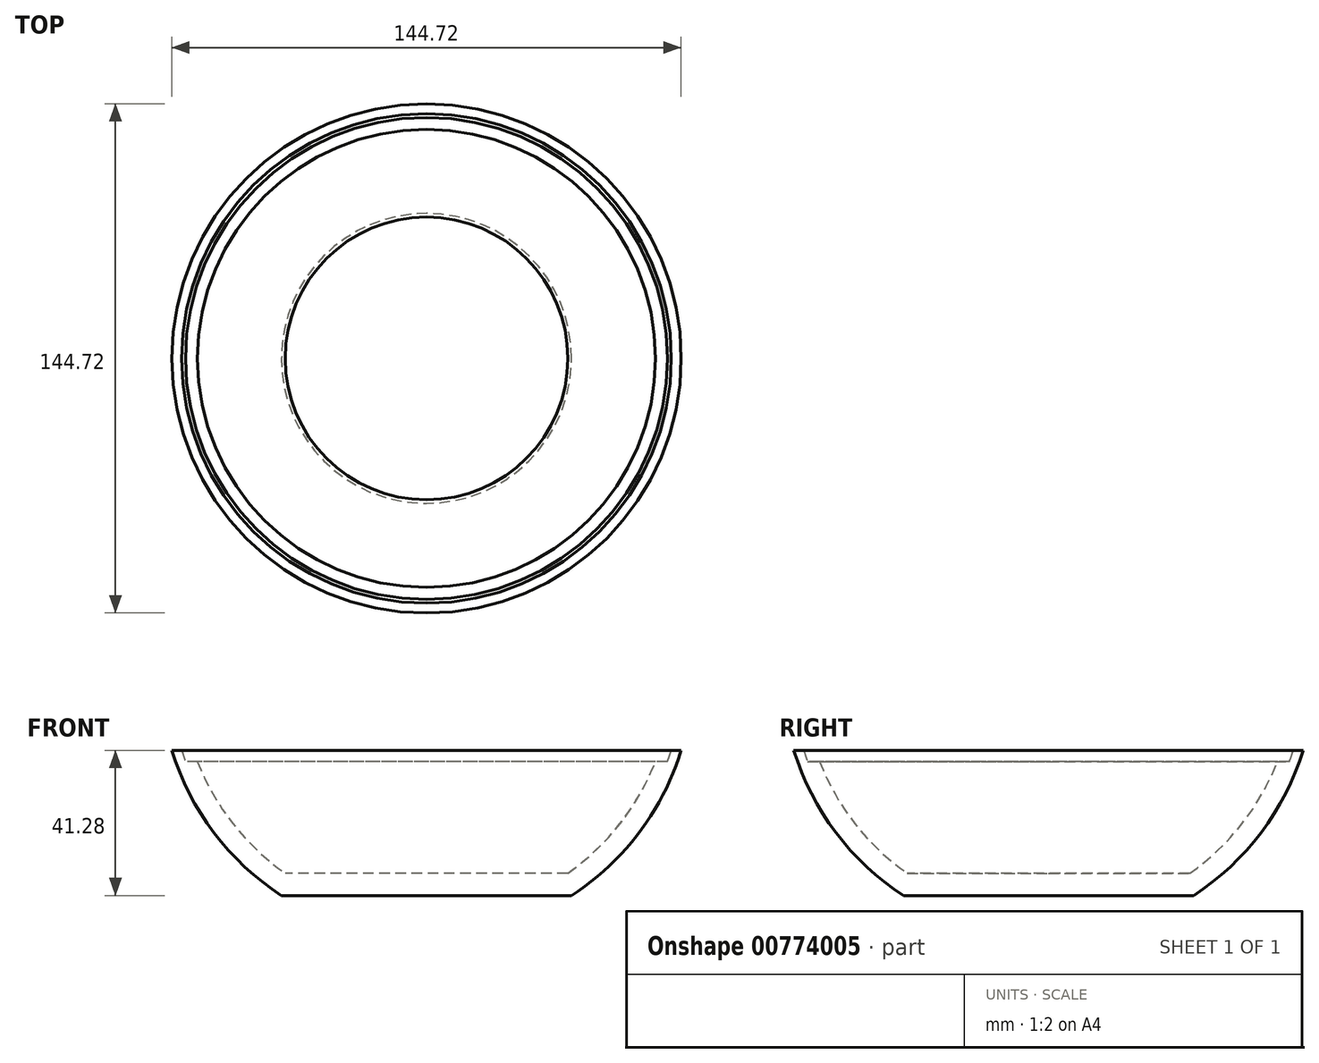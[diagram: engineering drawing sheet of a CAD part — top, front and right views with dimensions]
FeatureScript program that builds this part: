
annotation { "Feature Type Name" : "Feature", "Feature Type Description" : "" }
export const myFeature = defineFeature(function(context is Context, id is Id, definition is map)
    precondition{}
    {
        {
            var Q0;
            Q0=qCreatedBy(makeId("Front.planeOp"),FACE);
            var sketch = newSketch(context, id + "F0", { "sketchPlane" : qUnion([Q0])});
            skArc(sketch, "E0", {"start": v(-72.36, -22.23) * mm, "mid": v(-60.4, -45.6) * mm, "end": v(-41.2, -63.5) * mm});
            skLineSegment(sketch, "E1", {"start": v(-75.7, 0) * mm, "end": v(75.7, 0) * mm, "construction": true});
            skLineSegment(sketch, "E2.0", {"start": v(-72.36, -22.23) * mm, "end": v(-69.56, -22.23) * mm});
            skArc(sketch, "E3.0", {"start": v(-69.56, -22.23) * mm, "mid": v(-69.03, -23.82) * mm, "end": v(-68.47, -25.4) * mm});
            skArc(sketch, "E4.0", {"start": v(-65.07, -25.4) * mm, "mid": v(-54.96, -43.11) * mm, "end": v(-40.16, -57.15) * mm});
            skLineSegment(sketch, "E5.0", {"start": v(-68.47, -25.4) * mm, "end": v(-65.07, -25.4) * mm});
            skLineSegment(sketch, "E6", {"start": v(0, -57.15) * mm, "end": v(0, -63.5) * mm});
            skLineSegment(sketch, "E7.0", {"start": v(-41.2, -63.5) * mm, "end": v(0, -63.5) * mm});
            skLineSegment(sketch, "E8.0", {"start": v(-40.16, -57.15) * mm, "end": v(0, -57.15) * mm});
            skSolve(sketch);
        }
        {
            var Q0;
            Q0 = qSketchRegion(id + "F0", true);
            var Q1;
            Q1=sQuery(id+"F0.wireOp",EDGE,"E6");
            revolve(context, id + "F1", {"surfaceOperationType" : NewSurfaceOperationType.NEW, "entities" : qUnion([Q0]), "axis" : qUnion([Q1]), "revolveType" : RevolveType.FULL});
        }
    });
